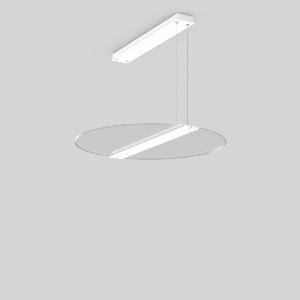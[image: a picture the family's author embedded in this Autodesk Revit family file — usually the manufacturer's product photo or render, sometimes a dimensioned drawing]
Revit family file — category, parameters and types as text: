
# Revit family: twindot_s_round_312353_002_1_76_4e2d
name_source: partatom
category: Lighting Fixtures
units: mm (PartAtom-declared; Revit-internal decimal feet)

## family parameters
Cut with Voids When Loaded = No
Host = Face
Light Source = No
Part Type = Normal
Room Calculation Point = No
Round Connector Dimension = Use Diameter
Shared = No

## types (1)
- TWINDOT S round (1 x LED Modul 840, 4500 lm, 4000)
    Apparent Load = 39 VA
    CIE Flux Codes = 49 78 94 56 100
    Color Rendering = 80
    Color Temperature = 4000
    Default Elevation = 1800 mm
    Description = Series: TWINDOT S round
LED pendant luminaire with extremely flat and frameless appearance. Middle bar made of aluminium extrusion profile, powder-coated. Transparent light guide made of UV-resistant acrylic glass (PMMA) with TWINDOT prismatic. Light control with perfectly glare-free TWINDOT technology for pleasantly gentle light with soft shadows. Even and wide indirect and direct light distribution. Direct 55%, indirect 45% light emission. 4-point steel cable suspension, steplessly adjustable. Converter integrated in the canopy (powder-coated white). Power supply through suspension cable. 
Colour: traffic white, matt (RAL 9016)
Diameter: 645 mm
Height: 20 mm
Suspension length: 500-1200 mm
Lamp: LED
Socket: without socket
Colour temperature: 4000K
Colour rendering index (CRI): 80
System power: 39 W
Rated luminous flux: 4500 lm
Luminous efficiency: 115 lm/W
Control gear: Converter, dimmable, DALI
Protection class: I
Type of protection: IP 20
    Height = 20 mm  [stored 0.0656168 ft]
    Lamp = 1 x LED Modul 840
    Lamp Light Flux = 4500 lm
    Lamp count = 1
    Length = 645 mm
    Lifetime = 50000 h
    Luminous efficacy = 115 lm/W
    Manufacturer = RZB
    ModVariant = No
    Model = 312353.002.1.76
    Mounting Place = Ceiling
    Mounting Type = Pendant
    Number of Poles = 1
    OnlyDefault = Yes
    Power Factor = 1
    Product Name = TWINDOT S round
    Product group = Pendant modular luminaires
    ProductGroupID = 906
    Protection Class = Protection class I
    Protection Degree = IP 20
    RLX_Detail_Level = 1
    RLX_Emergency_Light_Flux = 0 lm
    RLX_Emergency_Type = 0
    RLX_Emergency_Type_DB = No
    RlxData = <blob elided: 36229 chars, md5=ba1b5feb>
    Socket = socket
    Standby Power = 0 W
    System Light Flux = 4500 lm
    System Power = 39 W
    Type Comments = Product without accessories
    Type Image = 312353.002.jpg
    URL = http://relux.com
    VarID = ---
    Voltage = 230 V
    Voltage Range = 220-240 V
    Weight = 0.00 kg
    Width = 0 mm  [stored 0 ft]

note: [stored X ft] marks values corroborated as IEEE doubles in the binary element streams (Revit-internal decimal feet)

## geometry (parser evidence)
native form markers: Blend x4, Sweep x10
no freeform markers — native parametric forms only
